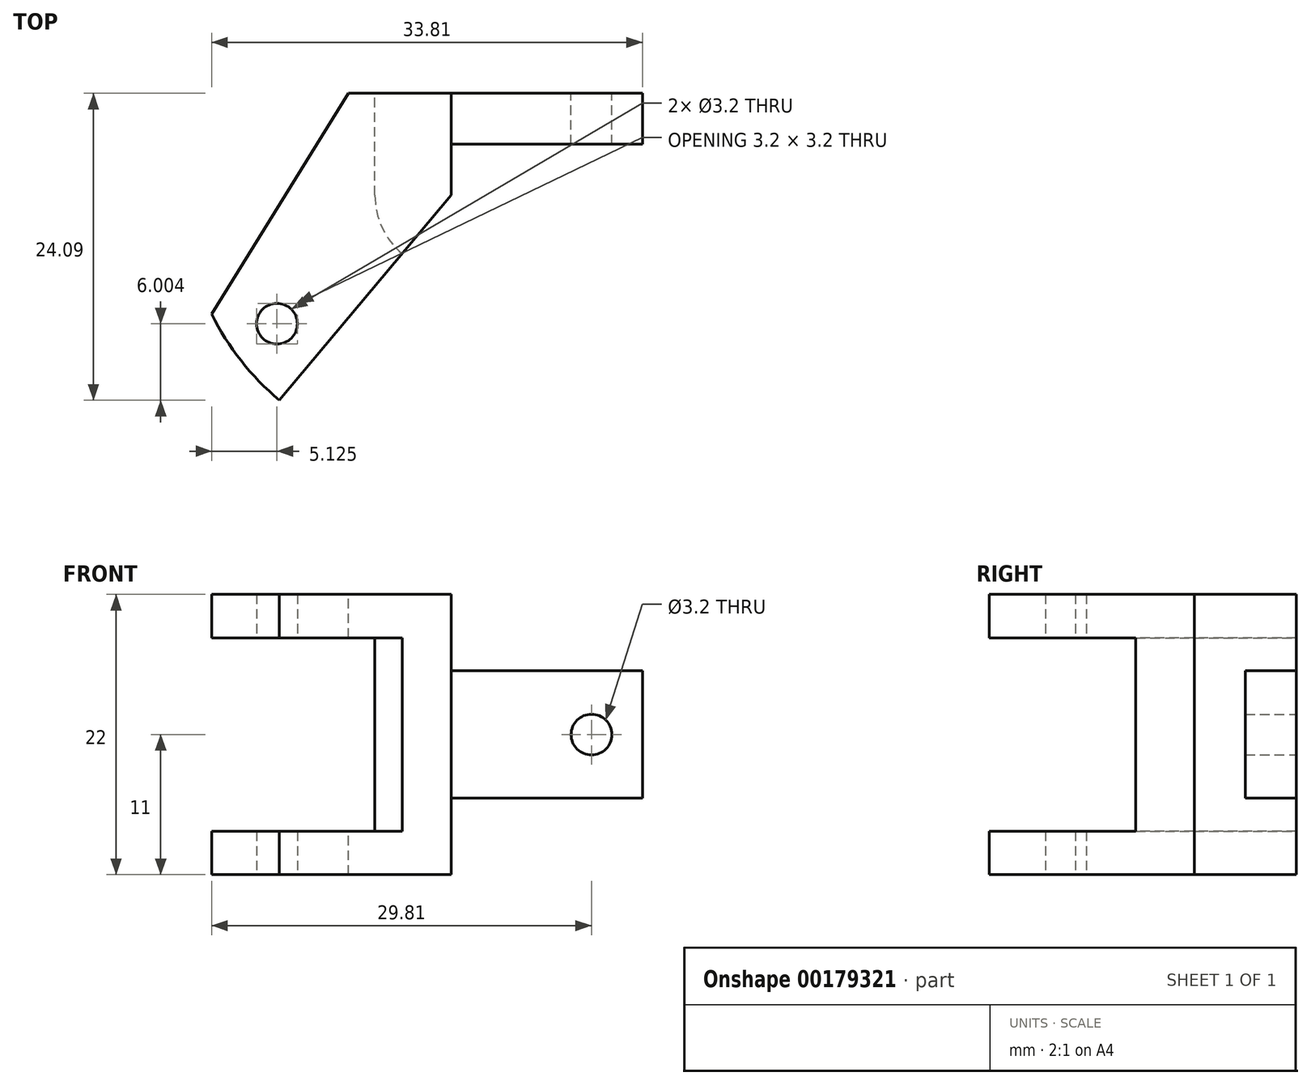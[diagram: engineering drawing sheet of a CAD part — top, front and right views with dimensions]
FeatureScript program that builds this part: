
annotation { "Feature Type Name" : "Feature", "Feature Type Description" : "" }
export const myFeature = defineFeature(function(context is Context, id is Id, definition is map)
    precondition{}
    {
        {
            var Q0;
            Q0=qCreatedBy(makeId("Front.planeOp"),FACE);
            var sketch = newSketch(context, id + "F0", { "sketchPlane" : qUnion([Q0])});
            skLineSegment(sketch, "E0", {"start": v(4, 0) * mm, "end": v(4, 5) * mm});
            skLineSegment(sketch, "E1", {"start": v(4, 5) * mm, "end": v(-11, 5) * mm});
            skLineSegment(sketch, "E2", {"start": v(-11, 5) * mm, "end": v(-11, 11) * mm});
            skLineSegment(sketch, "E3", {"start": v(-11, 11) * mm, "end": v(-32, 11) * mm});
            skLineSegment(sketch, "E4", {"start": v(-32, 11) * mm, "end": v(-32, 7.6) * mm});
            skLineSegment(sketch, "E5", {"start": v(-32, 7.6) * mm, "end": v(-17, 7.6) * mm});
            skLineSegment(sketch, "E6", {"start": v(-17, 7.6) * mm, "end": v(-17, 0) * mm});
            skLineSegment(sketch, "E7", {"start": v(-17, 0) * mm, "end": v(4, 0) * mm});
            skLineSegment(sketch, "E8.MirrorCS", {"start": v(-17, -7.6) * mm, "end": v(-17, 0) * mm});
            skLineSegment(sketch, "E9.MirrorCS", {"start": v(-32, -7.6) * mm, "end": v(-17, -7.6) * mm});
            skLineSegment(sketch, "E10.MirrorCS", {"start": v(-32, -11) * mm, "end": v(-32, -7.6) * mm});
            skLineSegment(sketch, "E11.MirrorCS", {"start": v(-11, -11) * mm, "end": v(-32, -11) * mm});
            skLineSegment(sketch, "E12.MirrorCS", {"start": v(-11, -5) * mm, "end": v(-11, -11) * mm});
            skLineSegment(sketch, "E13.MirrorCS", {"start": v(4, -5) * mm, "end": v(-11, -5) * mm});
            skLineSegment(sketch, "E14.MirrorCS", {"start": v(4, 0) * mm, "end": v(4, -5) * mm});
            skLineSegment(sketch, "E15", {"start": v(-11, 5) * mm, "end": v(-11, -5) * mm});
            skPoint(sketch, "E16", {"position": v(0, 0) * mm});
            skSolve(sketch);
        }
        {
            var Q0;
            {var subQ0=sQuery(id+"F0.wireOp",EDGE,"E0");Q0=makeQuery(id+"F0.imprint","IMPRINT",FACE,{"disambiguationData":[TD([[makeQuery(id+"F0.imprint","IMPRINT",EDGE,{"derivedFrom":subQ0}),1.0]])]});}
            var Q1;
            {var subQ4=sQuery(id+"F0.wireOp",EDGE,"E13.MirrorCS");Q1=makeQuery(id+"F0.imprint","IMPRINT",FACE,{"disambiguationData":[TD([[makeQuery(id+"F0.imprint","IMPRINT",EDGE,{"derivedFrom":subQ4}),-1.0]])]});}
            extrude(context, id + "F1", {"entities" : qUnion([Q0, Q1]), "depth" : 4 * mm});
        }
        {
            var Q0;
            {var subQ1=sQuery(id+"F0.wireOp",EDGE,"E2");Q0=makeQuery(id+"F0.imprint","IMPRINT",FACE,{"disambiguationData":[TD([[makeQuery(id+"F0.imprint","IMPRINT",EDGE,{"derivedFrom":subQ1}),1.0]])]});}
            var Q1;
            {var subQ0=sQuery(id+"F0.wireOp",EDGE,"E8.MirrorCS");Q1=makeQuery(id+"F0.imprint","IMPRINT",FACE,{"disambiguationData":[TD([[makeQuery(id+"F0.imprint","IMPRINT",EDGE,{"derivedFrom":subQ0}),-1.0]])]});}
            extrude(context, id + "F2", {"entities" : qUnion([Q0, Q1]), "operationType" : NewBodyOperationType.ADD, "depth" : 8 * mm});
        }
        {
            var Q0;
            Q0=makeQuery(id+"F2.opExtrude","CAP_FACE",FACE,{"disambiguationData":[OSD([sQuery(id+"F0.wireOp",EDGE,"E2"),sQuery(id+"F0.wireOp",EDGE,"E3"),sQuery(id+"F0.wireOp",EDGE,"E4"),sQuery(id+"F0.wireOp",EDGE,"E5"),sQuery(id+"F0.wireOp",EDGE,"E6"),sQuery(id+"F0.wireOp",EDGE,"E8.MirrorCS"),sQuery(id+"F0.wireOp",EDGE,"E9.MirrorCS"),sQuery(id+"F0.wireOp",EDGE,"E10.MirrorCS"),sQuery(id+"F0.wireOp",EDGE,"E11.MirrorCS"),sQuery(id+"F0.wireOp",EDGE,"E12.MirrorCS"),sQuery(id+"F0.wireOp",EDGE,"E15")])],"isStart":false});
            var Q1;
            Q1=makeQuery(id+"F2.opExtrude","CAP_EDGE",EDGE,{"disambiguationData":[OSD([sQuery(id+"F0.wireOp",EDGE,"E2"),sQuery(id+"F0.wireOp",EDGE,"E12.MirrorCS"),sQuery(id+"F0.wireOp",EDGE,"E15")])],"isStart":false});
            revolve(context, id + "F3", {"operationType" : NewBodyOperationType.ADD, "entities" : qUnion([Q0]), "axis" : qUnion([Q1]), "revolveType" : RevolveType.ONE_DIRECTION, "oppositeDirection" : true, "angle" : 50 * degree});
        }
        {
            var Q0;
            Q0=sQuery(id+"F0.wireOp",VERTEX,"E16");
            var Q1;
            Q1=makeQuery(id+"F1.opExtrude","SWEPT_BODY",BODY,{"disambiguationData":[OSD([sQuery(id+"F0.wireOp",EDGE,"E0"),sQuery(id+"F0.wireOp",EDGE,"E1"),sQuery(id+"F0.wireOp",EDGE,"E13.MirrorCS"),sQuery(id+"F0.wireOp",EDGE,"E14.MirrorCS"),sQuery(id+"F0.wireOp",EDGE,"E15")])]});
            hole(context, id + "F4", {"style" : HoleStyle.SIMPLE, "endStyle" : HoleEndStyle.THROUGH, "oppositeDirection" : true, "holeDiameter" : 3.2 * mm, "locations" : qUnion([Q0]), "scope" : qUnion([Q1]), "isTappedThrough" : true});
        }
        {
            var Q0;
            {var subQ0=sQuery(id+"F0.wireOp",EDGE,"E11.MirrorCS");Q0=makeQuery(id+"F3.boolean.opBoolean","MERGE",FACE,{"derivedFrom":[makeQuery(id+"F2.opExtrude","SWEPT_FACE",FACE,{"disambiguationData":[OSD([subQ0])]}),makeQuery(id+"F3.opRevolve","SWEPT_FACE",FACE,{"disambiguationData":[OSD([subQ0])]})]});}
            var sketch = newSketch(context, id + "F5", { "sketchPlane" : qUnion([Q0])});
            skPoint(sketch, "E17", {"position": v(-24.68, 18.09) * mm});
            skSolve(sketch);
        }
        {
            var Q0;
            Q0=sQuery(id+"F5.wireOp",VERTEX,"E17");
            var Q1;
            Q1=makeQuery(id+"F1.opExtrude","SWEPT_BODY",BODY,{"disambiguationData":[OSD([sQuery(id+"F0.wireOp",EDGE,"E0"),sQuery(id+"F0.wireOp",EDGE,"E1"),sQuery(id+"F0.wireOp",EDGE,"E13.MirrorCS"),sQuery(id+"F0.wireOp",EDGE,"E14.MirrorCS"),sQuery(id+"F0.wireOp",EDGE,"E15")])]});
            hole(context, id + "F6", {"style" : HoleStyle.SIMPLE, "endStyle" : HoleEndStyle.THROUGH, "holeDiameter" : 3.2 * mm, "locations" : qUnion([Q0]), "scope" : qUnion([Q1]), "isTappedThrough" : true});
        }
        {
            var Q0;
            Q0=makeQuery(id+"F2.opExtrude","CAP_EDGE",EDGE,{"disambiguationData":[OSD([sQuery(id+"F0.wireOp",EDGE,"E10.MirrorCS")])],"isStart":true});
            chamfer(context, id + "F7", {"entities" : qUnion([Q0]), "width" : 12 * mm, "tangentPropagation" : true});
        }
        {
            var Q0;
            Q0=makeQuery(id+"F2.opExtrude","CAP_EDGE",EDGE,{"disambiguationData":[OSD([sQuery(id+"F0.wireOp",EDGE,"E4")])],"isStart":true});
            chamfer(context, id + "F8", {"entities" : qUnion([Q0]), "width" : 12 * mm, "tangentPropagation" : true});
        }
    });
